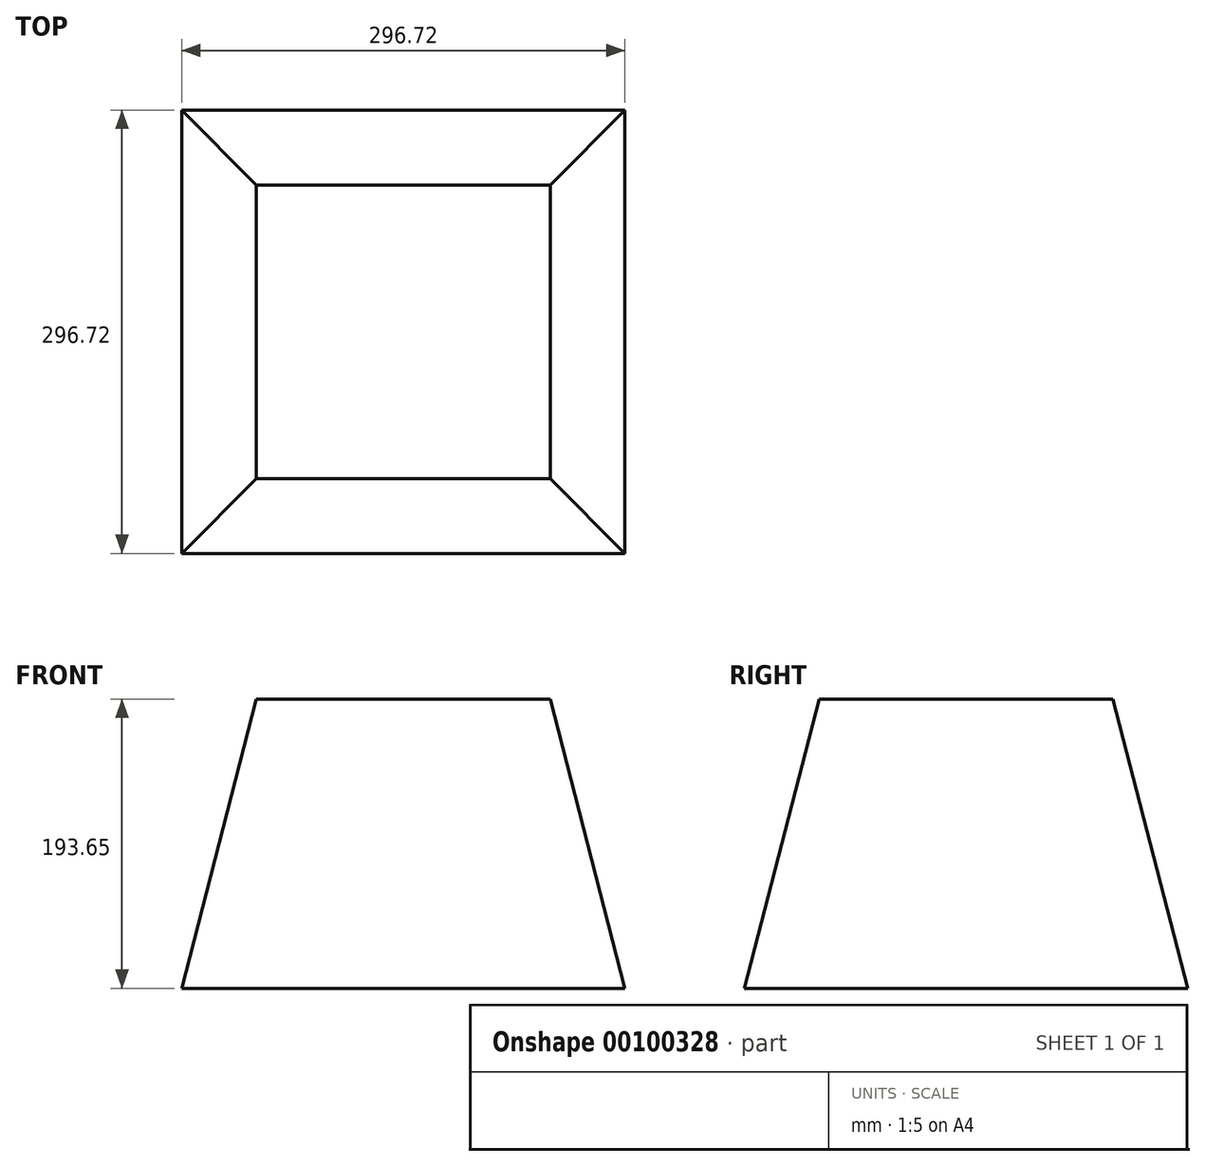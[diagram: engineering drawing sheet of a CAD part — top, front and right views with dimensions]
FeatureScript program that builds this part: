
annotation { "Feature Type Name" : "Feature", "Feature Type Description" : "" }
export const myFeature = defineFeature(function(context is Context, id is Id, definition is map)
    precondition{}
    {
        {
            var Q0;
            Q0=qCreatedBy(makeId("Front.planeOp"),FACE);
            var sketch = newSketch(context, id + "F0", { "sketchPlane" : qUnion([Q0])});
            skLineSegment(sketch, "E0.bottom", {"start": v(-148.12, 34.98) * mm, "end": v(151.88, 34.98) * mm});
            skLineSegment(sketch, "E0.top", {"start": v(-148.12, -158.67) * mm, "end": v(151.88, -158.67) * mm});
            skLineSegment(sketch, "E0.left", {"start": v(-148.12, 34.98) * mm, "end": v(-148.12, -158.67) * mm});
            skLineSegment(sketch, "E0.right", {"start": v(151.88, 34.98) * mm, "end": v(151.88, -158.67) * mm});
            skSolve(sketch);
        }
        {
            var Q0;
            Q0 = qSketchRegion(id + "F0", true);
            extrude(context, id + "F1", {"entities" : qUnion([Q0]), "depth" : 300 * mm});
        }
        {
            var Q0;
            Q0=makeQuery(id+"F1.opExtrude","SWEPT_FACE",FACE,{"disambiguationData":[OSD([sQuery(id+"F0.wireOp",EDGE,"E0.bottom")])]});
            chamfer(context, id + "F2", {"entities" : qUnion([Q0]), "chamferType" : ChamferType.OFFSET_ANGLE, "width" : 200 * mm, "oppositeDirection" : false, "angle" : 14.48 * degree});
        }
    });
